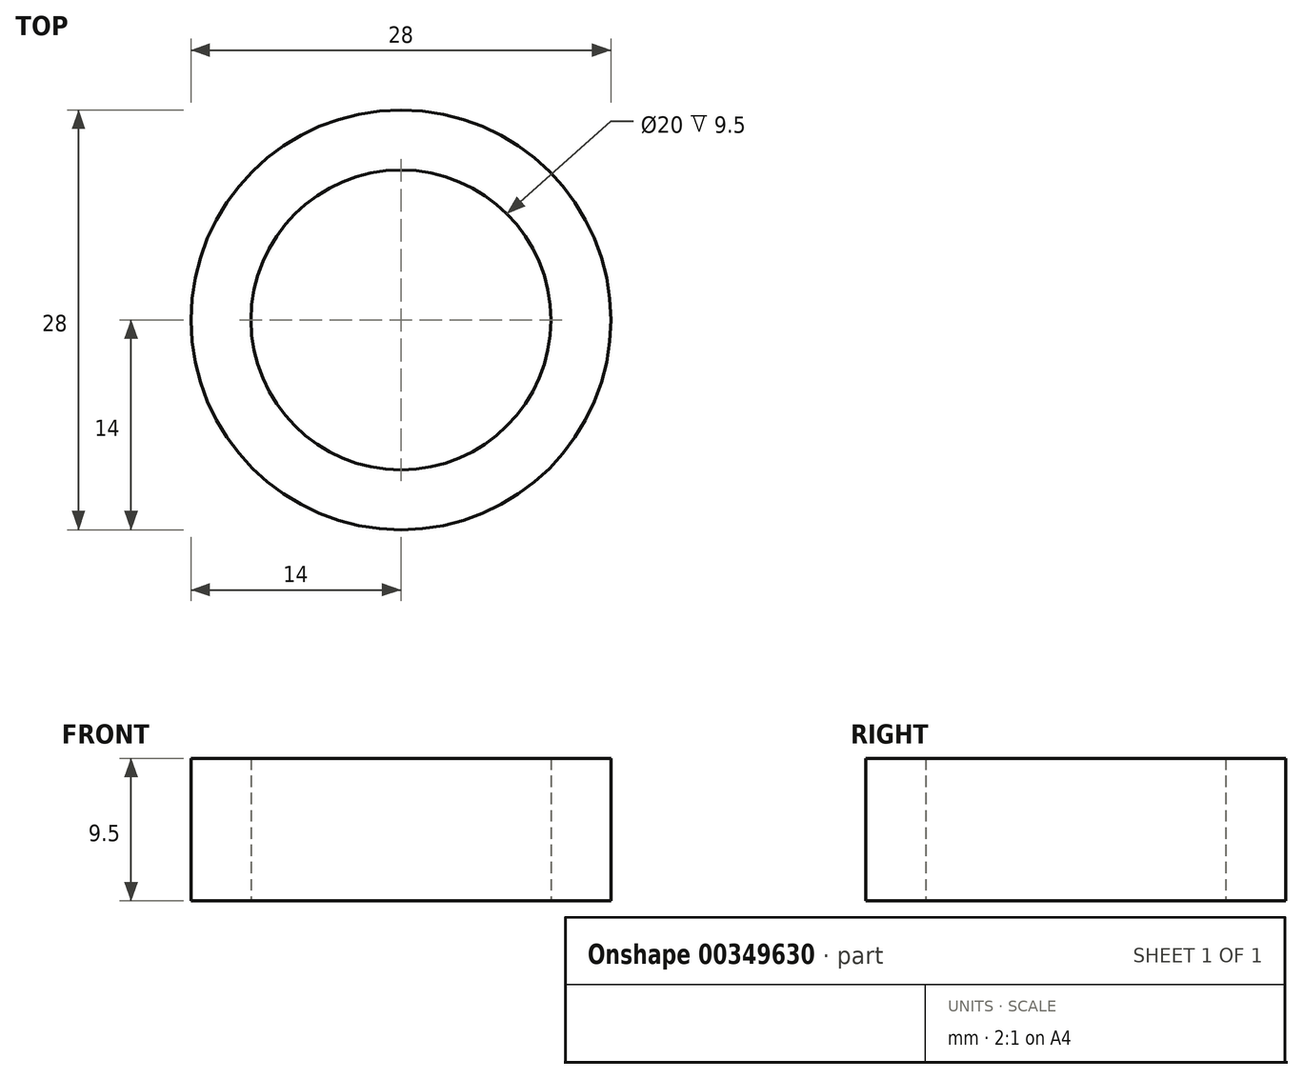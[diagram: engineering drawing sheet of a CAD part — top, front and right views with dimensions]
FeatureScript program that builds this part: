
annotation { "Feature Type Name" : "Feature", "Feature Type Description" : "" }
export const myFeature = defineFeature(function(context is Context, id is Id, definition is map)
    precondition{}
    {
        {
            var Q0;
            Q0=qCreatedBy(makeId("Top.planeOp"),FACE);
            var sketch = newSketch(context, id + "F0", { "sketchPlane" : qUnion([Q0])});
            skCircle(sketch, "E0", {"center": v(0, 0) * mm, "radius": 14 * mm});
            skCircle(sketch, "E1", {"center": v(0, 0) * mm, "radius": 10 * mm});
            skSolve(sketch);
        }
        {
            var Q0;
            Q0=makeQuery(id+"F0.imprint","IMPRINT",FACE,{"disambiguationData":[TD([[makeQuery(id+"F0.imprint","IMPRINT",EDGE,{"derivedFrom":sQuery(id+"F0.wireOp",EDGE,"E0")}),1.0]])]});
            extrude(context, id + "F1", {"entities" : qUnion([Q0]), "depth" : 9.5 * mm});
        }
    });
